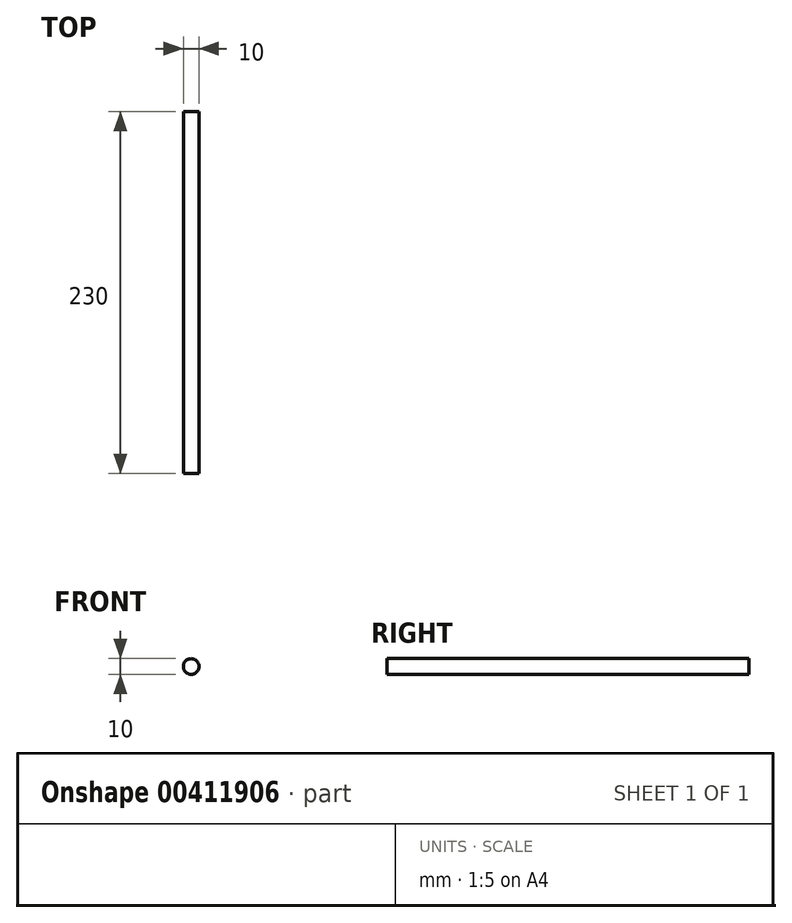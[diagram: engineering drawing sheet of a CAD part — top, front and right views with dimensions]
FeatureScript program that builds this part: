
annotation { "Feature Type Name" : "Feature", "Feature Type Description" : "" }
export const myFeature = defineFeature(function(context is Context, id is Id, definition is map)
    precondition{}
    {
        {
            var Q0;
            Q0=qCreatedBy(makeId("Front.planeOp"),FACE);
            var sketch = newSketch(context, id + "F0", { "sketchPlane" : qUnion([Q0])});
            skCircle(sketch, "E0", {"center": v(0, 0) * mm, "radius": 5 * mm});
            skSolve(sketch);
        }
        {
            var Q0;
            Q0 = qSketchRegion(id + "F0", true);
            extrude(context, id + "F1", {"entities" : qUnion([Q0]), "endBound" : BoundingType.SYMMETRIC, "depth" : 230 * mm});
        }
    });
